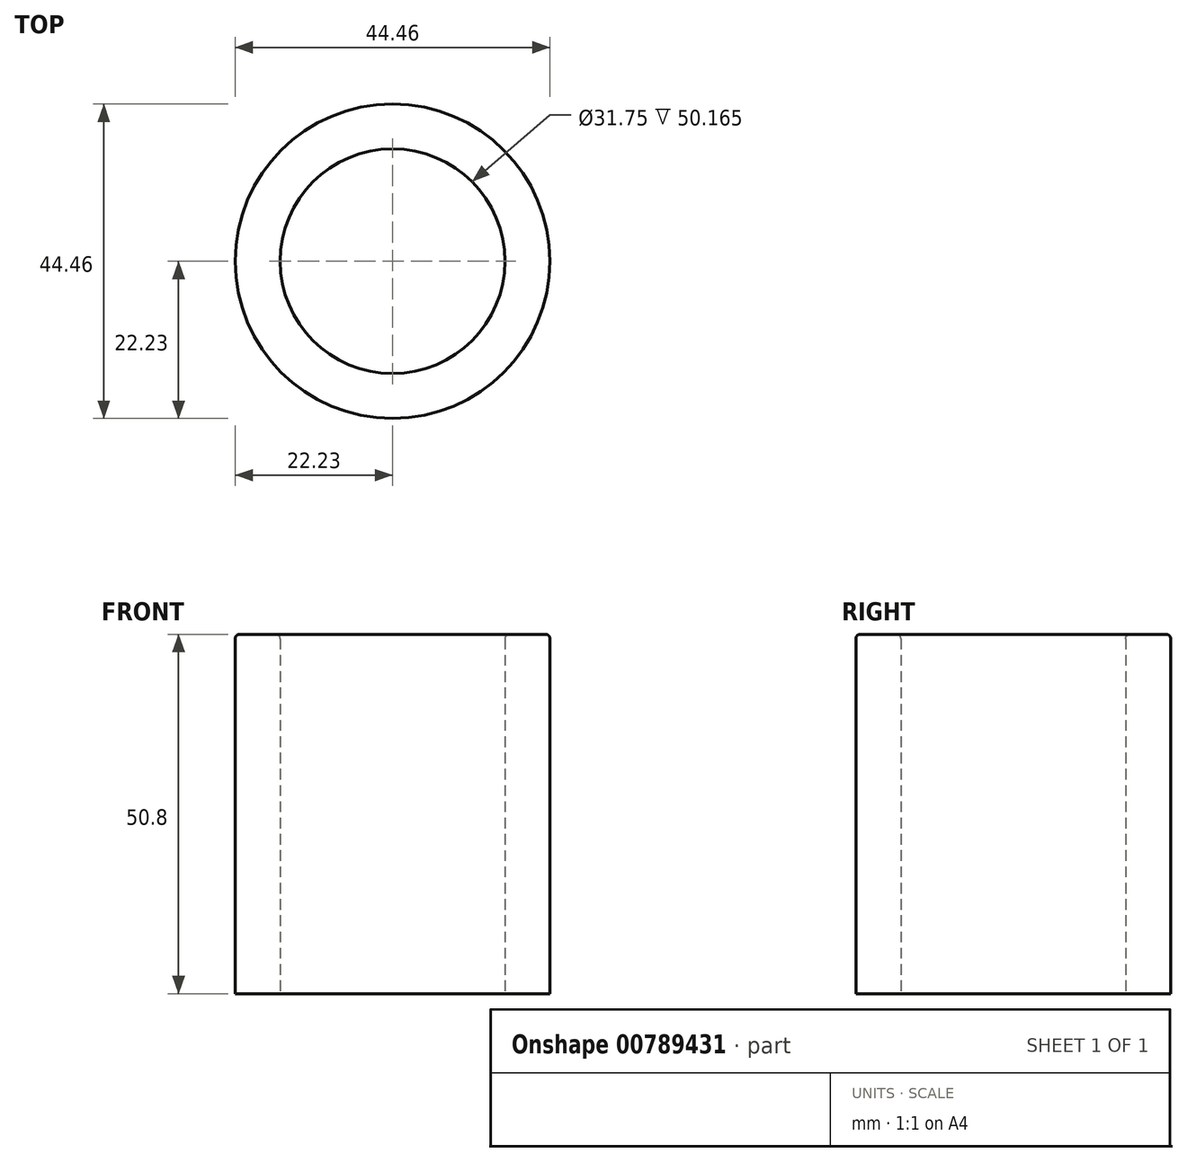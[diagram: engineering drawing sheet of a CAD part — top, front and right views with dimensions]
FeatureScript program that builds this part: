
annotation { "Feature Type Name" : "Feature", "Feature Type Description" : "" }
export const myFeature = defineFeature(function(context is Context, id is Id, definition is map)
    precondition{}
    {
        {
            var Q0;
            Q0=qCreatedBy(makeId("Top.planeOp"),FACE);
            var sketch = newSketch(context, id + "F0", { "sketchPlane" : qUnion([Q0])});
            skCircle(sketch, "E0", {"center": v(0, 0) * mm, "radius": 22.23 * mm});
            skSolve(sketch);
        }
        {
            var Q0;
            Q0 = qSketchRegion(id + "F0", true);
            extrude(context, id + "F1", {"entities" : qUnion([Q0]), "depth" : 50.8 * mm, "offsetDistance" : 25.4 * mm});
        }
        {
            var Q0;
            Q0=makeQuery(id+"F1.opExtrude","CAP_FACE",FACE,{"disambiguationData":[OSD([sQuery(id+"F0.wireOp",EDGE,"E0")])],"isStart":false});
            var Q1;
            Q1=makeQuery(id+"F1.opExtrude","CAP_FACE",FACE,{"disambiguationData":[OSD([sQuery(id+"F0.wireOp",EDGE,"E0")])],"isStart":true});
            shell(context, id + "F2", {"entities" : qUnion([Q0, Q1]), "thickness" : 6.35 * mm});
        }
        {
            var Q0;
            Q0=makeQuery(id+"F1.opExtrude","CAP_EDGE",EDGE,{"disambiguationData":[OSD([sQuery(id+"F0.wireOp",EDGE,"E0")])],"isStart":false});
            var Q1;
            {var subQ0=sQuery(id+"F0.wireOp",EDGE,"E0");Q1=makeQuery(id+"F2.opShell","OFFSET_EDGE",EDGE,{"disambiguationData":[OSD([subQ0]),TDD([makeQuery(id+"F1.opExtrude","CAP_EDGE",EDGE,{"disambiguationData":[OSD([subQ0])],"isStart":false})])]});}
            fillet(context, id + "F3", {"entities" : qUnion([Q0, Q1]), "radius" : 0.64 * mm, "tangentPropagation" : true, "allowEdgeOverflow" : false});
        }
    });
